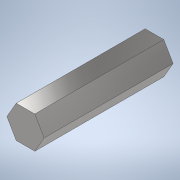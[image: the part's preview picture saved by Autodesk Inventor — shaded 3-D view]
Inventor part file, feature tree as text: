
AUTODESK INVENTOR PART (.ipt)
format: ipt  version: 2020 (Build 240168000, 168)  size: 97,792 bytes
history: native  units: in
note: dims shown in document units (in); Inventor stores cm internally (conversion verified against a paired STEP export)
features: extrude x1, sketch x1
ambient origin geometry x8: Origin, YZ Plane, XZ Plane, XY Plane, X Axis, Y Axis, Z Axis, Center Point
bodies: Solid1 (feature_tree)
feature tree (2):
  extrude  "Extrusion1"  Depth=2.0in TaperAngle=0.0deg
  sketch  "Sketch1"  dims[d0=0.5in d1=2.0in d2=0.0in]
